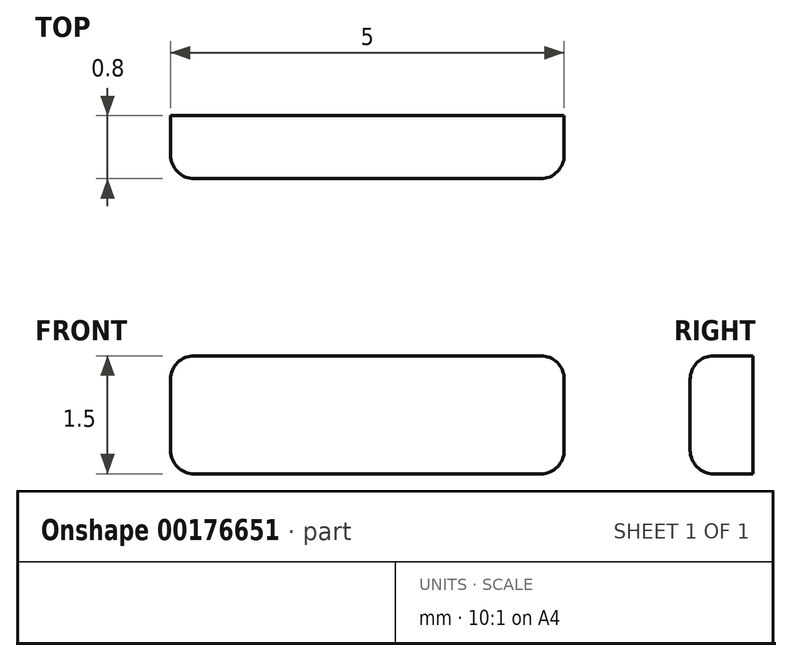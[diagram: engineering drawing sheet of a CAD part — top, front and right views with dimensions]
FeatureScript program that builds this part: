
annotation { "Feature Type Name" : "Feature", "Feature Type Description" : "" }
export const myFeature = defineFeature(function(context is Context, id is Id, definition is map)
    precondition{}
    {
        {
            var Q0;
            Q0=qCreatedBy(makeId("Front.planeOp"),FACE);
            var sketch = newSketch(context, id + "F0", { "sketchPlane" : qUnion([Q0])});
            skLineSegment(sketch, "E0.bottom", {"start": v(2.5, 0.75) * mm, "end": v(-2.5, 0.75) * mm});
            skLineSegment(sketch, "E0.top", {"start": v(2.5, -0.75) * mm, "end": v(-2.5, -0.75) * mm});
            skLineSegment(sketch, "E0.left", {"start": v(2.5, 0.75) * mm, "end": v(2.5, -0.75) * mm});
            skLineSegment(sketch, "E0.right", {"start": v(-2.5, 0.75) * mm, "end": v(-2.5, -0.75) * mm});
            skPoint(sketch, "E0.middle", {"position": v(0, 0) * mm});
            skSolve(sketch);
        }
        {
            var Q0;
            Q0 = qSketchRegion(id + "F0", true);
            extrude(context, id + "F1", {"entities" : qUnion([Q0]), "depth" : 0.8 * mm});
        }
        {
            var Q0;
            Q0=makeQuery(id+"F1.opExtrude","CAP_EDGE",EDGE,{"disambiguationData":[OSD([sQuery(id+"F0.wireOp",EDGE,"E0.bottom")])],"isStart":false});
            var Q1;
            Q1=makeQuery(id+"F1.opExtrude","SWEPT_EDGE",EDGE,{"disambiguationData":[OSD([sQuery(id+"F0.wireOp",EDGE,"E0.bottom"),sQuery(id+"F0.wireOp",EDGE,"E0.right")])]});
            var Q2;
            Q2=makeQuery(id+"F1.opExtrude","SWEPT_EDGE",EDGE,{"disambiguationData":[OSD([sQuery(id+"F0.wireOp",EDGE,"E0.bottom"),sQuery(id+"F0.wireOp",EDGE,"E0.left")])]});
            var Q3;
            Q3=makeQuery(id+"F1.opExtrude","CAP_EDGE",EDGE,{"disambiguationData":[OSD([sQuery(id+"F0.wireOp",EDGE,"E0.right")])],"isStart":false});
            var Q4;
            Q4=makeQuery(id+"F1.opExtrude","CAP_EDGE",EDGE,{"disambiguationData":[OSD([sQuery(id+"F0.wireOp",EDGE,"E0.left")])],"isStart":false});
            var Q5;
            Q5=makeQuery(id+"F1.opExtrude","SWEPT_EDGE",EDGE,{"disambiguationData":[OSD([sQuery(id+"F0.wireOp",EDGE,"E0.top"),sQuery(id+"F0.wireOp",EDGE,"E0.left")])]});
            var Q6;
            Q6=makeQuery(id+"F1.opExtrude","CAP_EDGE",EDGE,{"disambiguationData":[OSD([sQuery(id+"F0.wireOp",EDGE,"E0.top")])],"isStart":false});
            var Q7;
            Q7=makeQuery(id+"F1.opExtrude","SWEPT_EDGE",EDGE,{"disambiguationData":[OSD([sQuery(id+"F0.wireOp",EDGE,"E0.top"),sQuery(id+"F0.wireOp",EDGE,"E0.right")])]});
            fillet(context, id + "F2", {"entities" : qUnion([Q0, Q1, Q2, Q3, Q4, Q5, Q6, Q7]), "radius" : 0.3 * mm, "tangentPropagation" : true, "allowEdgeOverflow" : false});
        }
    });
